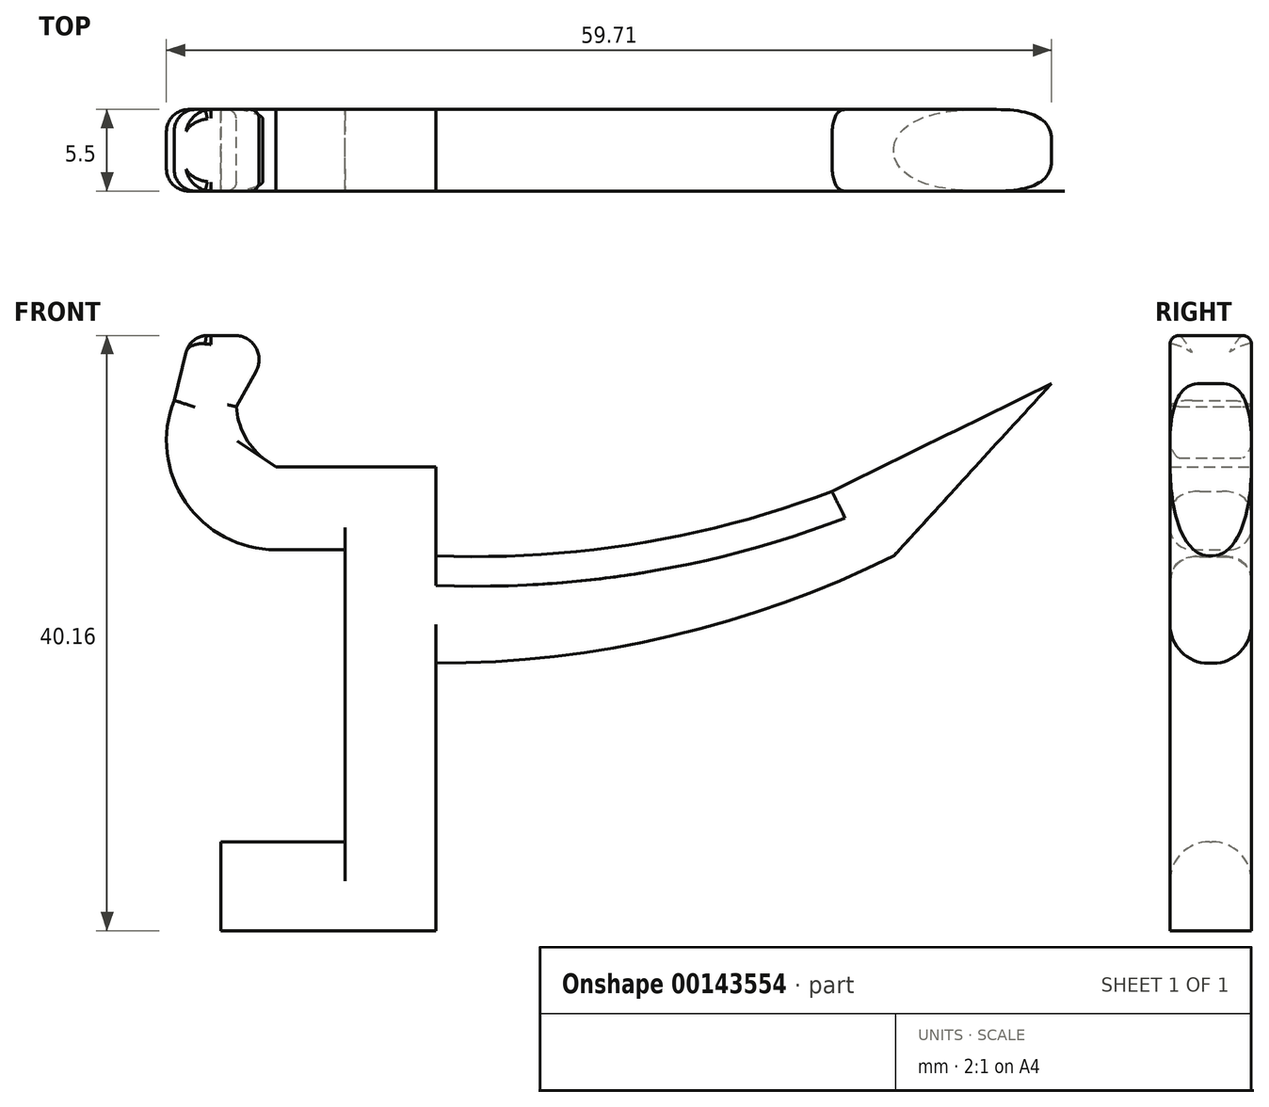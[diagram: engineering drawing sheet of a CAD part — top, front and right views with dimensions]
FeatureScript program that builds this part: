
annotation { "Feature Type Name" : "Feature", "Feature Type Description" : "" }
export const myFeature = defineFeature(function(context is Context, id is Id, definition is map)
    precondition{}
    {
        {
            var Q0;
            Q0=qCreatedBy(makeId("Front.planeOp"),FACE);
            var sketch = newSketch(context, id + "F0", { "sketchPlane" : qUnion([Q0])});
            skLineSegment(sketch, "E0.bottom", {"start": v(0, 0) * mm, "end": v(2.2, 0) * mm});
            skLineSegment(sketch, "E0.top", {"start": v(0, 6) * mm, "end": v(2.2, 6) * mm});
            skLineSegment(sketch, "E0.left", {"start": v(0, 0) * mm, "end": v(0, 6) * mm});
            skLineSegment(sketch, "E0.right", {"start": v(2.2, 0) * mm, "end": v(2.2, 6) * mm});
            skLineSegment(sketch, "E1.bottom", {"start": v(0, 6) * mm, "end": v(-4.66, 6) * mm});
            skLineSegment(sketch, "E1.top", {"start": v(0, 0.4) * mm, "end": v(-4.66, 0.4) * mm});
            skLineSegment(sketch, "E1.left", {"start": v(0, 6) * mm, "end": v(0, 0.4) * mm});
            skLineSegment(sketch, "E1.right", {"start": v(-4.66, 6) * mm, "end": v(-4.66, 0.4) * mm});
            skArc(sketch, "E2", {"start": v(-4.66, 14.86) * mm, "mid": v(-7.34, 10.43) * mm, "end": v(-4.66, 6) * mm});
            skArc(sketch, "E3", {"start": v(-8.84, 13.86) * mm, "mid": v(-11.7, 5.6) * mm, "end": v(-4.66, 0.4) * mm});
            skLineSegment(sketch, "E4", {"start": v(-4.66, 14.86) * mm, "end": v(-10.43, 14.86) * mm});
            skLineSegment(sketch, "E5", {"start": v(-10.43, 14.86) * mm, "end": v(-12, 8.6) * mm});
            skLineSegment(sketch, "E6", {"start": v(-4.66, 14.86) * mm, "end": v(-8.25, 8.4) * mm});
            skLineSegment(sketch, "E7", {"start": v(-8.25, 8.4) * mm, "end": v(-4.66, 6) * mm});
            skLineSegment(sketch, "E8.bottom", {"start": v(0, 6) * mm, "end": v(6.15, 6) * mm});
            skLineSegment(sketch, "E8.top", {"start": v(0, -7.26) * mm, "end": v(6.15, -7.26) * mm});
            skLineSegment(sketch, "E8.left", {"start": v(0, 6) * mm, "end": v(0, -7.26) * mm});
            skLineSegment(sketch, "E8.right", {"start": v(6.15, 6) * mm, "end": v(6.15, -7.26) * mm});
            skArc(sketch, "E9", {"start": v(6.15, -7.26) * mm, "mid": v(22.02, -5.42) * mm, "end": v(37.05, 0) * mm});
            skArc(sketch, "E10", {"start": v(6.15, 0) * mm, "mid": v(19.73, 0.81) * mm, "end": v(32.86, 4.34) * mm});
            skPoint(sketch, "E10.startSnap0", {"position": v(6.15, -0.63) * mm});
            skLineSegment(sketch, "E11", {"start": v(37.05, 0) * mm, "end": v(47.67, 11.61) * mm});
            skLineSegment(sketch, "E12", {"start": v(47.67, 11.61) * mm, "end": v(32.86, 4.34) * mm});
            skLineSegment(sketch, "E13.bottom", {"start": v(0, -7.26) * mm, "end": v(6.11, -7.26) * mm});
            skLineSegment(sketch, "E13.left", {"start": v(0, -7.26) * mm, "end": v(0, -22.3) * mm});
            skLineSegment(sketch, "E14", {"start": v(0, 3.2) * mm, "end": v(0, -22.3) * mm, "construction": true});
            skLineSegment(sketch, "E15.bottom", {"start": v(-8.37, -19.3) * mm, "end": v(6.15, -19.3) * mm});
            skLineSegment(sketch, "E15.top", {"start": v(-8.37, -25.3) * mm, "end": v(6.15, -25.3) * mm});
            skLineSegment(sketch, "E15.left", {"start": v(-8.37, -19.3) * mm, "end": v(-8.37, -25.3) * mm});
            skPoint(sketch, "E15.middle", {"position": v(0, -22.3) * mm});
            skLineSegment(sketch, "E16", {"start": v(6.15, -7.26) * mm, "end": v(6.15, -25.3) * mm});
            skLineSegment(sketch, "E17", {"start": v(6.15, -25.3) * mm, "end": v(-8.37, -25.3) * mm});
            skPoint(sketch, "E15.right.start.orphan", {"position": v(8.37, -19.3) * mm});
            skPoint(sketch, "E18.orphan", {"position": v(8.37, -25.3) * mm});
            skSolve(sketch);
        }
        {
            var Q0;
            Q0 = qSketchRegion(id + "F0", true);
            extrude(context, id + "F1", {"entities" : qUnion([Q0]), "depth" : 5.5 * mm});
        }
        {
            var Q0;
            Q0=makeQuery(id+"F1.opExtrude","CAP_EDGE",EDGE,{"disambiguationData":[OSD([sQuery(id+"F0.wireOp",EDGE,"E10")])],"isStart":false});
            var Q1;
            Q1=makeQuery(id+"F1.opExtrude","CAP_EDGE",EDGE,{"disambiguationData":[OSD([sQuery(id+"F0.wireOp",EDGE,"E12")])],"isStart":false});
            var Q2;
            Q2=makeQuery(id+"F1.opExtrude","CAP_EDGE",EDGE,{"disambiguationData":[OSD([sQuery(id+"F0.wireOp",EDGE,"E12")])],"isStart":true});
            var Q3;
            Q3=makeQuery(id+"F1.opExtrude","CAP_EDGE",EDGE,{"disambiguationData":[OSD([sQuery(id+"F0.wireOp",EDGE,"E10")])],"isStart":true});
            fillet(context, id + "F2", {"entities" : qUnion([Q0, Q1, Q2, Q3]), "radius" : 2 * mm, "tangentPropagation" : true, "rho" : 0.5, "crossSection" : FilletCrossSection.CONIC, "allowEdgeOverflow" : false});
        }
        {
            var Q0;
            Q0=makeQuery(id+"F1.opExtrude","CAP_EDGE",EDGE,{"disambiguationData":[OSD([sQuery(id+"F0.wireOp",EDGE,"E15.bottom")])],"isStart":false});
            var Q1;
            Q1=makeQuery(id+"F1.opExtrude","CAP_EDGE",EDGE,{"disambiguationData":[OSD([sQuery(id+"F0.wireOp",EDGE,"E15.bottom")])],"isStart":true});
            var Q2;
            Q2=makeQuery(id+"F1.opExtrude","CAP_EDGE",EDGE,{"disambiguationData":[OSD([sQuery(id+"F0.wireOp",EDGE,"E17")])],"isStart":true});
            var Q3;
            Q3=makeQuery(id+"F1.opExtrude","CAP_EDGE",EDGE,{"disambiguationData":[OSD([sQuery(id+"F0.wireOp",EDGE,"E17")])],"isStart":false});
            fillet(context, id + "F3", {"entities" : qUnion([Q0, Q1, Q2, Q3]), "radius" : 2.66 * mm, "tangentPropagation" : true, "allowEdgeOverflow" : false});
        }
        {
            var Q0;
            Q0=makeQuery(id+"F1.opExtrude","SWEPT_EDGE",EDGE,{"disambiguationData":[OSD([sQuery(id+"F0.wireOp",EDGE,"E2"),sQuery(id+"F0.wireOp",EDGE,"E4"),sQuery(id+"F0.wireOp",EDGE,"E6")])]});
            fillet(context, id + "F4", {"entities" : qUnion([Q0]), "radius" : 1.62 * mm, "tangentPropagation" : true, "allowEdgeOverflow" : false});
        }
        {
            var Q0;
            Q0=makeQuery(id+"F1.opExtrude","CAP_EDGE",EDGE,{"disambiguationData":[OSD([sQuery(id+"F0.wireOp",EDGE,"E2")])],"isStart":true});
            var Q1;
            Q1=makeQuery(id+"F1.opExtrude","CAP_EDGE",EDGE,{"disambiguationData":[OSD([sQuery(id+"F0.wireOp",EDGE,"E2")])],"isStart":false});
            var Q2;
            Q2=makeQuery(id+"F1.opExtrude","CAP_EDGE",EDGE,{"disambiguationData":[OSD([sQuery(id+"F0.wireOp",EDGE,"E6")])],"isStart":false});
            var Q3;
            Q3=makeQuery(id+"F1.opExtrude","CAP_EDGE",EDGE,{"disambiguationData":[OSD([sQuery(id+"F0.wireOp",EDGE,"E6")])],"isStart":true});
            fillet(context, id + "F5", {"entities" : qUnion([Q0, Q1, Q2, Q3]), "radius" : .6 * mm, "tangentPropagation" : true, "allowEdgeOverflow" : false});
        }
        {
            var Q0;
            Q0=makeQuery(id+"F1.opExtrude","CAP_EDGE",EDGE,{"disambiguationData":[OSD([sQuery(id+"F0.wireOp",EDGE,"E3")])],"isStart":true});
            var Q1;
            Q1=makeQuery(id+"F1.opExtrude","CAP_EDGE",EDGE,{"disambiguationData":[OSD([sQuery(id+"F0.wireOp",EDGE,"E5")])],"isStart":true});
            var Q2;
            Q2=makeQuery(id+"F1.opExtrude","CAP_EDGE",EDGE,{"disambiguationData":[OSD([sQuery(id+"F0.wireOp",EDGE,"E1.top")])],"isStart":false});
            var Q3;
            Q3=makeQuery(id+"F1.opExtrude","CAP_EDGE",EDGE,{"disambiguationData":[OSD([sQuery(id+"F0.wireOp",EDGE,"E3")])],"isStart":false});
            var Q4;
            Q4=makeQuery(id+"F1.opExtrude","CAP_EDGE",EDGE,{"disambiguationData":[OSD([sQuery(id+"F0.wireOp",EDGE,"E5")])],"isStart":false});
            var Q5;
            Q5=makeQuery(id+"F1.opExtrude","CAP_EDGE",EDGE,{"disambiguationData":[OSD([sQuery(id+"F0.wireOp",EDGE,"E1.top")])],"isStart":true});
            fillet(context, id + "F6", {"entities" : qUnion([Q0, Q1, Q2, Q3, Q4, Q5]), "radius" : 1.49 * mm, "tangentPropagation" : true, "allowEdgeOverflow" : false});
        }
        {
            var Q0;
            Q0=makeQuery(id+"F1.opExtrude","CAP_EDGE",EDGE,{"disambiguationData":[OSD([sQuery(id+"F0.wireOp",EDGE,"E9")])],"isStart":true});
            var Q1;
            Q1=makeQuery(id+"F1.opExtrude","CAP_EDGE",EDGE,{"disambiguationData":[OSD([sQuery(id+"F0.wireOp",EDGE,"E9")])],"isStart":false});
            fillet(context, id + "F7", {"entities" : qUnion([Q0, Q1]), "radius" : 2.6 * mm, "tangentPropagation" : true, "allowEdgeOverflow" : false});
        }
    });
